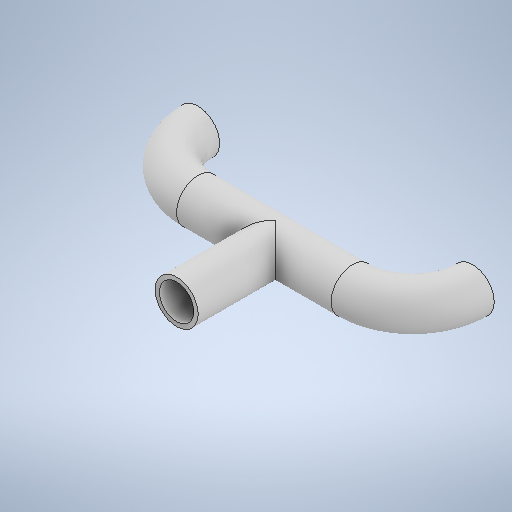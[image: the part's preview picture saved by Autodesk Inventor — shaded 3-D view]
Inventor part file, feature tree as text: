
AUTODESK INVENTOR PART (.ipt)
format: ipt  version: 2025.1 (Build 291241000, 241)  size: 312,832 bytes
history: native  units: mm
features: sketch x3, sweep x1, plane x1, extrude x1
ambient origin geometry x8: Origin, YZ Plane, XZ Plane, XY Plane, X Axis, Y Axis, Z Axis, Center Point
bodies: Solid1 (feature_tree)
feature tree (6):
  sweep  "Sweep1"
  plane  "Work Plane1"
  extrude  "Extrusion1"  Depth=7.0mm
  sketch  "Sketch1"  dims[d0=5.0mm d1=4.0mm]
  sketch  "Sketch2"  dims[d3=32.0mm d4=7.0mm]
  sketch  "Sketch3"  dims[d5=7.0mm d6=0.0mm d7=0.0mm d8=-18.5mm d9=5.0mm d10=16.0mm d11=4.0mm d12=10.0mm d13=0.0mm]
